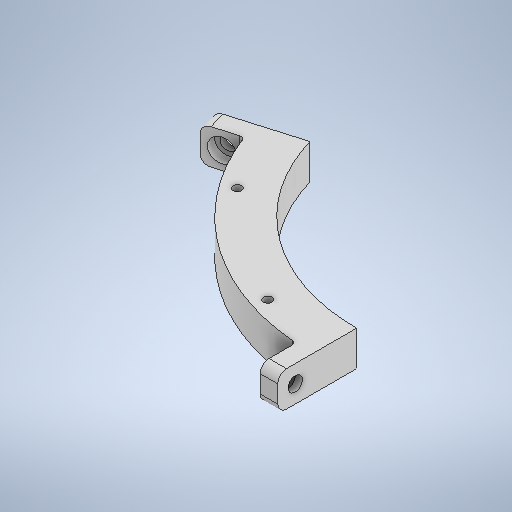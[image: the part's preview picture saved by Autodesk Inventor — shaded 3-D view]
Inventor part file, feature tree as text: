
AUTODESK INVENTOR PART (.ipt)
format: ipt  version: 2025 (Build 290162000, 162)  size: 384,512 bytes
history: native  units: in
note: dims shown in document units (in); Inventor stores cm internally (conversion verified against a paired STEP export)
features: sketch x12, extrude x8, hole x3, fillet x2
ambient origin geometry x8: Origin, YZ Plane, XZ Plane, XY Plane, X Axis, Y Axis, Z Axis, Center Point
bodies: Solid1 (feature_tree)
feature tree (25):
  extrude  "Extrusion1"  Depth=8.6614in
  extrude  "Extrusion2"  Depth=1.4173in
  hole  "Hole1"  [1 undecoded]
  extrude  "Extrusion3"  Depth=0.1575in TaperAngle=360.0deg
  extrude  "Extrusion7"  Depth=0.1575in TaperAngle=0.0deg
  extrude  "Extrusion8"  Depth=2.7559in
  extrude  "Extrusion9"  Depth=0.7874in
  fillet  "Fillet1"  Radius=0.5906in
  hole  "Hole2"  [1 undecoded]
  extrude  "Extrusion10"  Depth=0.7874in
  fillet  "Fillet2"  Radius=0.1969in
  extrude  "Extrusion11"  Depth=0.0984in
  hole  "Hole3"  [1 undecoded]
  sketch  "Sketch1"  dims[d0=10.6299in d1=8.6614in]
  sketch  "Sketch2"  dims[d5=0.0in d6=0.0in d7=10.0394in]
  sketch  "Sketch3"  dims[d8=0.1575in d9=3.937in d11=360.0deg]
  sketch  "Sketch Circular Pattern1"  dims[d2=1.8504in d3=0.0in d4=1.4173in]
  sketch  "Sketch4"  dims[d13=0.1969in d14=0.3937in d15=0.1575in d16=0.0787in d17=90.0deg d18=0.5591in d19=0.8108in d20=1.063in d21=0.0in]
  sketch  "Sketch7"  dims[d38=0.1181in d39=2.7559in]
  sketch  "Sketch8"  dims[d40=0.7874in d41=7.874in d42=0.5906in d43=0.0in]
  sketch  "Sketch9"  dims[d44=0.0in d45=0.0in d46=0.8858in]
  sketch  "Sketch10"  dims[d47=0.7874in d48=0.7874in d49=0.1969in]
  sketch  "Sketch11"  dims[d50=0.3937in d51=0.0in d52=0.0984in]
  sketch  "Sketch12"  dims[d53=0.3937in d54=0.3937in]
  sketch  "Sketch13"  dims[d55=0.3228in d56=0.2362in d57=0.5197in d58=0.2362in d59=90.0deg d60=0.315in d61=0.8108in d62=0.8858in d63=0.7874in d64=0.7874in d65=0.1969in d66=0.3937in d67=0.0in d68=0.0984in d69=0.3937in d70=0.3937in d71=0.5197in d72=0.2362in d73=0.0in d74=0.3937in d75=0.3228in d76=0.2362in d77=0.5197in d78=0.2362in d79=90.0deg d80=0.315in d81=0.8108in d30=0.0197in d31=0.0344in d32=0.0197in d33=0.0344in]
note: 3 required parameter values undecoded (feature->parameter linkage not recoverable at this tier; creation-order binding heuristic only, values carry confidence <= 0.55)
